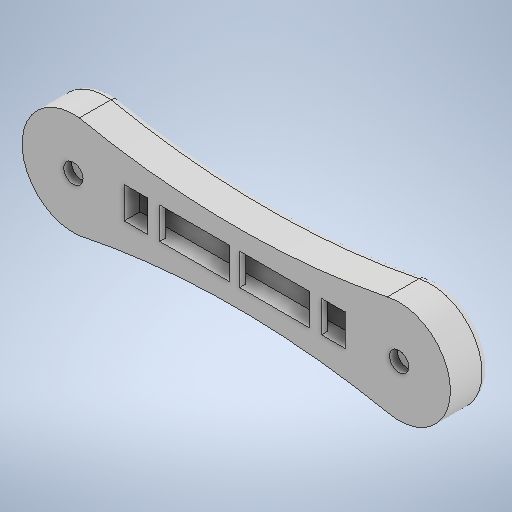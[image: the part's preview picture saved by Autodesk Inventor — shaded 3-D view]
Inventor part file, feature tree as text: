
AUTODESK INVENTOR PART (.ipt)
format: ipt  version: 2025.2 (Build 292293000, 293)  size: 673,792 bytes
history: native  units: mm
features: extrude x4, sketch x3, other x1, fillet x1
ambient origin geometry x8: Origin, YZ Plane, XZ Plane, XY Plane, X Axis, Y Axis, Z Axis, Center Point
bodies: Body1 (feature_tree)
feature tree (9):
  other  "Bryła1"
  sketch  "Szkic1"
  extrude  "Wyciągnięcie proste1"  Depth=13.0mm
  extrude  "Wyciągnięcie proste2"  Depth=13.0mm
  fillet  "Zaokrąglenie1"  Radius=194.164878mm
  extrude  "Wyciągnięcie proste3"  Depth=194.164878mm
  extrude  "Wyciągnięcie proste4"  Depth=20.0mm
  sketch  "Szkic2"
  sketch  "Szkic3"
